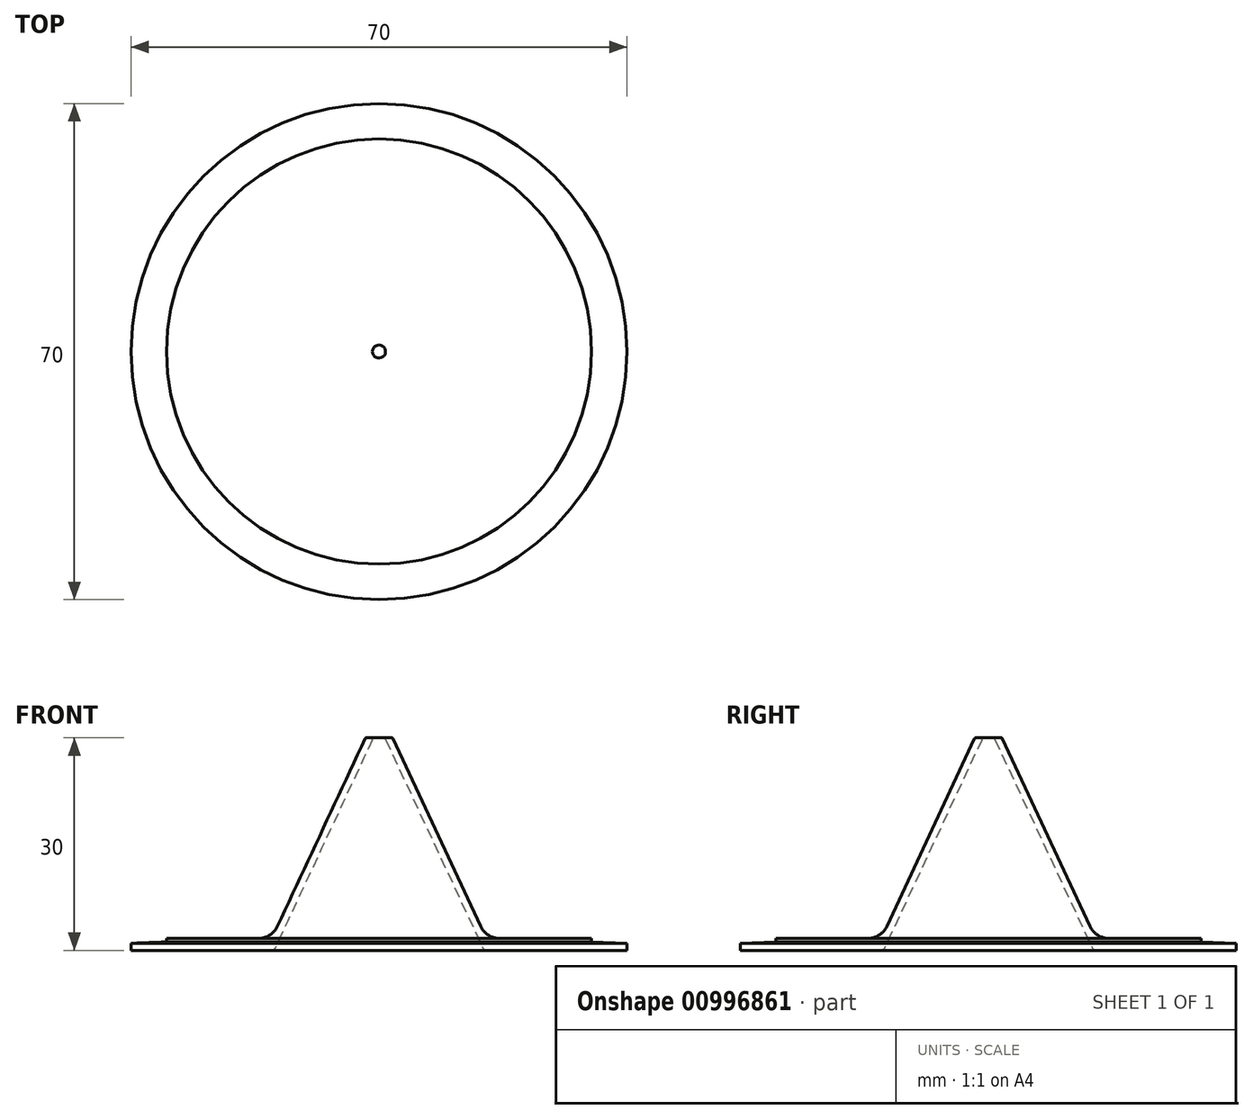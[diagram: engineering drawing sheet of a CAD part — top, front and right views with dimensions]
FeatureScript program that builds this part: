
annotation { "Feature Type Name" : "Feature", "Feature Type Description" : "" }
export const myFeature = defineFeature(function(context is Context, id is Id, definition is map)
    precondition{}
    {
        {
            var Q0;
            Q0=qCreatedBy(makeId("Front.planeOp"),FACE);
            var sketch = newSketch(context, id + "F0", { "sketchPlane" : qUnion([Q0])});
            skLineSegment(sketch, "E0.bottom", {"start": v(15.13, 0) * mm, "end": v(35, 0) * mm});
            skLineSegment(sketch, "E0.right", {"start": v(35, 0) * mm, "end": v(35, 1) * mm});
            skLineSegment(sketch, "E1.top", {"start": v(15.13, 1.67) * mm, "end": v(30, 1.67) * mm});
            skLineSegment(sketch, "E1.left", {"start": v(-0.2, 1) * mm, "end": v(-0.2, 1.67) * mm});
            skLineSegment(sketch, "E1.right", {"start": v(30, 1.17) * mm, "end": v(30, 1.67) * mm});
            skLineSegment(sketch, "E2.top", {"start": v(1.12, 30) * mm, "end": v(1.79, 30) * mm});
            skLineSegment(sketch, "E3", {"start": v(0.94, 29.72) * mm, "end": v(14.67, 0.29) * mm});
            skLineSegment(sketch, "E4.0", {"start": v(1.97, 29.88) * mm, "end": v(15.13, 1.67) * mm});
            skLineSegment(sketch, "E5.trimOffspring", {"start": v(30, 1.17) * mm, "end": v(35, 1) * mm});
            skPoint(sketch, "E6.orphan", {"position": v(-0.2, 30) * mm});
            skPoint(sketch, "E7.visualSharp", {"position": v(1.91, 30) * mm});
            skArc(sketch, "E7.filletArc", {"start": v(1.97, 29.88) * mm, "mid": v(1.9, 29.97) * mm, "end": v(1.79, 30) * mm});
            skPoint(sketch, "E8.visualSharp", {"position": v(0.8, 30) * mm});
            skArc(sketch, "E8.filletArc", {"start": v(1.12, 30) * mm, "mid": v(0.95, 29.9) * mm, "end": v(0.94, 29.72) * mm});
            skPoint(sketch, "E9.visualSharp", {"position": v(14.8, 0) * mm});
            skArc(sketch, "E9.filletArc", {"start": v(14.67, 0.29) * mm, "mid": v(14.86, 0.08) * mm, "end": v(15.13, 0) * mm});
            skLineSegment(sketch, "E10.left", {"start": v(0, 0) * mm, "end": v(0, 32.51) * mm});
            skSolve(sketch);
        }
        {
            var Q0;
            Q0=makeQuery(id+"F0.imprint","IMPRINT",FACE,{"disambiguationData":[TD([[makeQuery(id+"F0.imprint","IMPRINT",EDGE,{"derivedFrom":sQuery(id+"F0.wireOp",EDGE,"E0.bottom")}),1.0]])]});
            var Q1;
            Q1=sQuery(id+"F0.wireOp",EDGE,"E10.left");
            revolve(context, id + "F1", {"surfaceOperationType" : NewSurfaceOperationType.NEW, "entities" : qUnion([Q0]), "axis" : qUnion([Q1]), "revolveType" : RevolveType.FULL});
        }
        {
            var Q0;
            Q0=makeQuery(id+"F1.opRevolve","SWEPT_EDGE",EDGE,{"disambiguationData":[OSD([sQuery(id+"F0.wireOp",EDGE,"E1.top"),sQuery(id+"F0.wireOp",EDGE,"E4.0")])]});
            fillet(context, id + "F2", {"entities" : qUnion([Q0]), "radius" : 3 * mm, "tangentPropagation" : true, "allowEdgeOverflow" : false});
        }
    });
